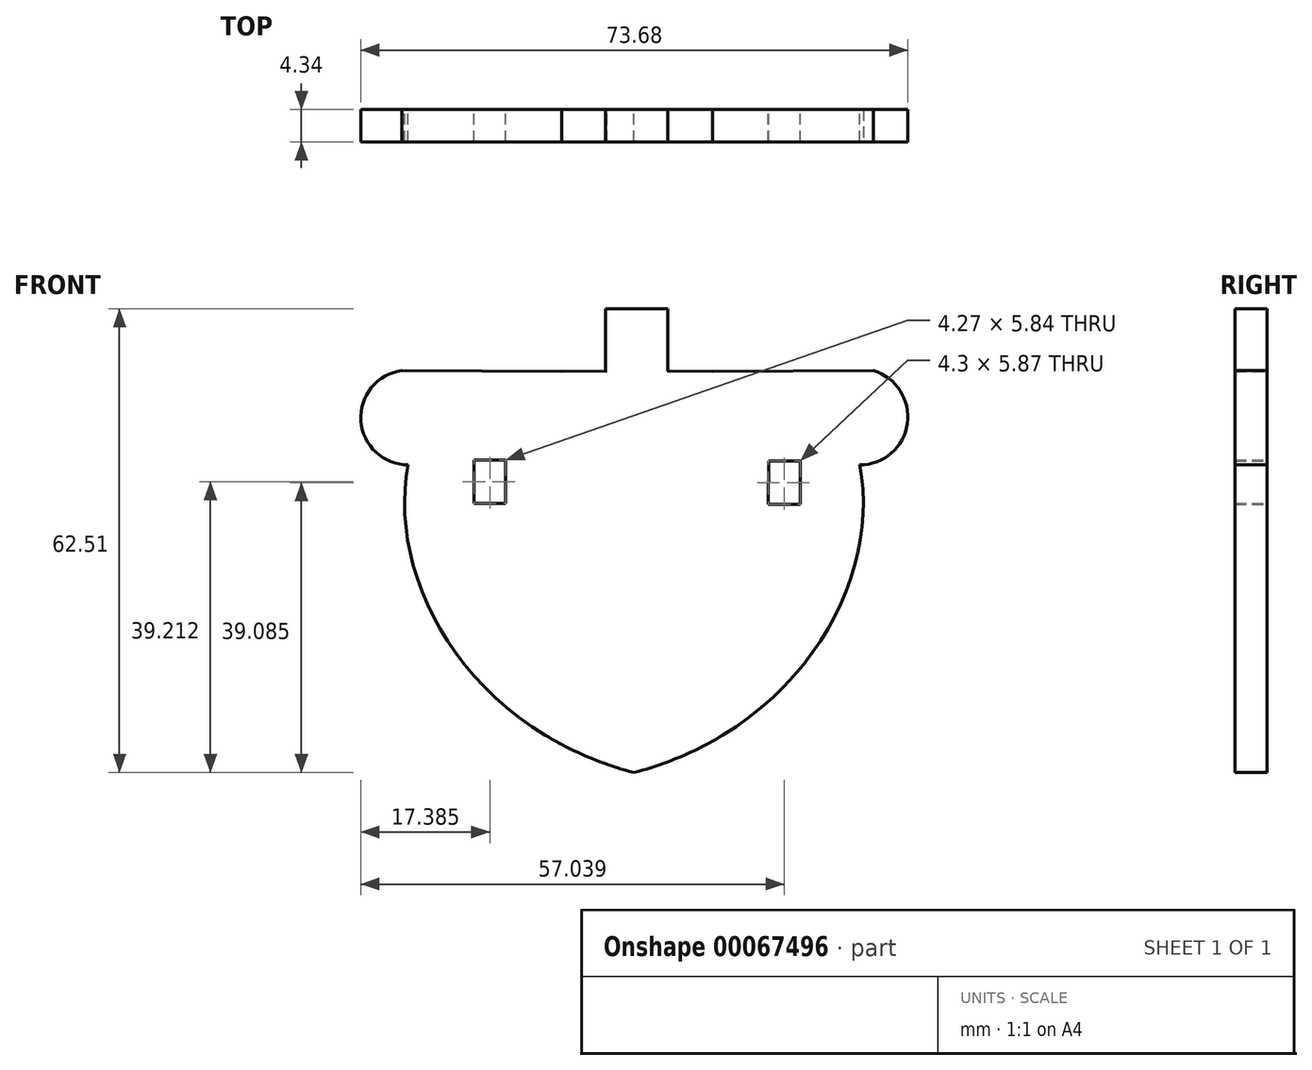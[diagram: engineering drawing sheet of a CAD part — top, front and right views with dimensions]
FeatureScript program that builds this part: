
annotation { "Feature Type Name" : "Feature", "Feature Type Description" : "" }
export const myFeature = defineFeature(function(context is Context, id is Id, definition is map)
    precondition{}
    {
        {
            var Q0;
            Q0=qCreatedBy(makeId("Front.planeOp"),FACE);
            var sketch = newSketch(context, id + "F0", { "sketchPlane" : qUnion([Q0])});
            skLineSegment(sketch, "E0.0", {"start": v(-18.48, -1.73) * mm, "end": v(42.34, -1.73) * mm, "construction": true});
            skArc(sketch, "E1", {"start": v(-19.35, 10.97) * mm, "mid": v(-24.84, 4.21) * mm, "end": v(-18.48, -1.73) * mm});
            skArc(sketch, "E2", {"start": v(42.34, -1.73) * mm, "mid": v(48.76, 3.84) * mm, "end": v(44.15, 10.97) * mm});
            skFitSpline(sketch, "E3", {"points": [v(-18.48, -1.73) * mm, v(14.82, -43.88) * mm, v(585.84, 287.03) * mm], "startDerivative": vector(-42.26, -216.85) * mm, "endDerivative": vector(953.24, 643.91) * mm});
            skPoint(sketch, "E4.top.start.orphan", {"position": v(-7.46, -49.2) * mm});
            skPoint(sketch, "E5.orphan", {"position": v(37.1, -38.56) * mm});
            skPoint(sketch, "E6.orphan", {"position": v(27.34, -41.18) * mm});
            skPoint(sketch, "E7.start.orphan", {"position": v(11.93, -1.73) * mm});
            skFitSpline(sketch, "E8.MirrorCS", {"points": [v(42.34, -1.73) * mm, v(9.05, -43.88) * mm, v(-561.97, 287.03) * mm], "startDerivative": vector(42.26, -216.85) * mm, "endDerivative": vector(-953.24, 643.91) * mm});
            skLineSegment(sketch, "E9", {"start": v(12.4, 10.97) * mm, "end": v(12.24, -38.16) * mm});
            skPoint(sketch, "E10.middle", {"position": v(12.32, 12.12) * mm});
            skLineSegment(sketch, "E11", {"start": v(-19.35, 10.97) * mm, "end": v(2.16, 10.85) * mm});
            skLineSegment(sketch, "E12", {"start": v(22.48, 10.85) * mm, "end": v(44.15, 10.97) * mm});
            skPoint(sketch, "E13.MirrorCS.start.orphan", {"position": v(45.57, 7.16) * mm});
            skLineSegment(sketch, "E14.bottom", {"start": v(-5.34, -6.9) * mm, "end": v(-9.6, -6.9) * mm});
            skLineSegment(sketch, "E14.top", {"start": v(-5.34, -1.07) * mm, "end": v(-9.6, -1.07) * mm});
            skLineSegment(sketch, "E14.left", {"start": v(-5.34, -6.9) * mm, "end": v(-5.34, -1.07) * mm});
            skLineSegment(sketch, "E14.right", {"start": v(-9.6, -6.9) * mm, "end": v(-9.6, -1.07) * mm});
            skPoint(sketch, "E14.middle", {"position": v(-7.48, -3.99) * mm});
            skLineSegment(sketch, "E15.MirrorCS", {"start": v(30.06, -1.18) * mm, "end": v(34.33, -1.2) * mm});
            skLineSegment(sketch, "E16.MirrorCS", {"start": v(30.03, -7.02) * mm, "end": v(34.3, -7.05) * mm});
            skLineSegment(sketch, "E17.MirrorCS", {"start": v(34.3, -7.05) * mm, "end": v(34.33, -1.2) * mm});
            skLineSegment(sketch, "E18", {"start": v(30.06, -1.18) * mm, "end": v(30.03, -7.02) * mm});
            skLineSegment(sketch, "E19.bottom", {"start": v(8.37, -30.5) * mm, "end": v(15.23, -30.5) * mm});
            skLineSegment(sketch, "E19.left", {"start": v(8.37, -30.5) * mm, "end": v(8.37, -38.12) * mm});
            skLineSegment(sketch, "E19.right", {"start": v(15.23, -30.5) * mm, "end": v(15.23, -38.12) * mm});
            skLineSegment(sketch, "E20", {"start": v(0, -38.16) * mm, "end": v(8.37, -38.12) * mm});
            skLineSegment(sketch, "E21", {"start": v(15.23, -38.12) * mm, "end": v(23.87, -38.16) * mm});
            skLineSegment(sketch, "E22.top", {"start": v(12.37, 10.93) * mm, "end": v(12.4, 10.93) * mm});
            skPoint(sketch, "E10.left.end.orphan", {"position": v(22.48, 13.4) * mm});
            skPoint(sketch, "E10.right.end.orphan", {"position": v(2.16, 13.4) * mm});
            skPoint(sketch, "E23", {"position": v(12.37, 10.93) * mm});
            skLineSegment(sketch, "E24", {"start": v(2.16, 10.85) * mm, "end": v(8.94, 10.93) * mm});
            skLineSegment(sketch, "E25", {"start": v(15.8, 10.93) * mm, "end": v(22.48, 10.85) * mm});
            skLineSegment(sketch, "E26.bottom", {"start": v(8.12, 19.3) * mm, "end": v(16.5, 19.3) * mm});
            skLineSegment(sketch, "E26.top", {"start": v(8.12, 10.92) * mm, "end": v(8.3, 10.92) * mm});
            skLineSegment(sketch, "E26.left", {"start": v(8.12, 19.3) * mm, "end": v(8.12, 10.92) * mm});
            skLineSegment(sketch, "E26.right", {"start": v(16.5, 19.3) * mm, "end": v(16.5, 10.92) * mm});
            skPoint(sketch, "E27", {"position": v(12.3, 10.92) * mm});
            skLineSegment(sketch, "E28.trimOffspring", {"start": v(16.43, 10.92) * mm, "end": v(16.5, 10.92) * mm});
            skLineSegment(sketch, "E29.trimOffspring", {"start": v(12.3, 10.92) * mm, "end": v(12.4, 10.92) * mm});
            skSolve(sketch);
        }
        {
            var Q0;
            Q0 = qSketchRegion(id + "F0", true);
            extrude(context, id + "F1", {"entities" : qUnion([Q0]), "depth" : 4.34 * mm});
        }
    });
